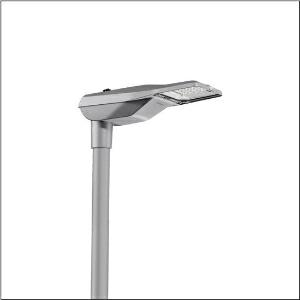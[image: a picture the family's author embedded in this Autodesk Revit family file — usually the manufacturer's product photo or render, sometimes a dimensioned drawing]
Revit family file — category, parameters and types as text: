
# Revit family: streetlight_sl_21_micro___st1_5a_5xe1p43s08db_ce40
name_source: partatom
category: Lighting Fixtures
units: mm (PartAtom-declared; Revit-internal decimal feet)

## family parameters
Cut with Voids When Loaded = No
Host = Face
Light Source = No
Part Type = Normal
Room Calculation Point = No
Round Connector Dimension = Use Diameter
Shared = No

## types (1)
- --- (1 x LED, 5230 lm, 39.1 W, 4000K)
    Apparent Load = 39 VA
    CIE Flux Codes = 22 53 95 100 100
    Color Rendering = 70
    Color Temperature = 4000K
    Default Elevation = 1800 mm
    Description = Streetlight SL 21 micro, mast luminaire, primary light control with lens, of PMMA, primary optical cover: cover, of toughened safety glass, transparent, light distribution: ST1.5a, light emission: direct distribution, primary light characteristic: asymmetric, installation type: side-entry, post-top, LED, High Power LED, rated luminous flux: 5.230lm, luminous efficacy: 134lm/W, light colour: 740, colour temperature: 4000K, control: flexible luminous flux parameterisation, time-dependent luminous flux control, constant luminous flux control, overheat protection, pre-setting: logarithmic dimming characteristic, mains connection: 220..240V, AC, 50/60Hz, start of lifetime: 39W, end of service life: 41W, reduction: 18W, luminaire housing, of diecast aluminium, powder-coated, Siteco® metallic grey (DB 702S), corrosivity category C5 mid according to DIN EN ISO 12944, please order mast flange separately, inclination adjustable: 0°, 5°, 10°, 15°, sealing non-destructively replaceable, multi-level sealing system, length: 528mm, width: 235mm, height: 110mm, mast flange for spigot size: 42mm (side-entry): 5XC10008XM4, 60/48mm (side-entry/post-top): 5XC10108XM2, 76/60mm (side-entry/post-top): 5XC10108XM1, Smart Interface above, protection rating (complete): IP66, insulation class (complete): insulation class II (safety insulation), certification: CE, ENEC, ENEC+, VDE, impact resistance: IK09, permissible operating ambient temperature for outdoor applications: -40..+50°C, standard-compliant lighting for roads and squares, packaging unit: 1 piece

Light Distribution: ST1.5a
    Height = 110 mm
    Lamp = 1 x LED
    Lamp Light Flux = 5230 lm
    Lamp Power = 39.1 W
    Lamp count = 1
    Length = 528 mm
    Luminous efficacy = 134 lm/W
    Manufacturer = Siteco
    ModVariant = No
    Model = 5XE1P43S08DB
    Number of Poles = 1
    OnlyDefault = Yes
    Power Factor = 1
    Product Name = Streetlight SL 21 micro | ST1.5a
    Product group = mast luminaire | pylon top
    ProductGroupID = 6100
    Protection Class = Protection class II
    Protection Degree = IP 66
    RLX_Detail_Level = 1
    RLX_Emergency_Light_Flux = 0 lm
    RLX_Emergency_Type = 0
    RLX_Emergency_Type_DB = No
    RlxData = <blob elided: 102553 chars, md5=652c07a2>
    Socket = socket
    Standby Power = 0 W
    System Light Flux = 5230 lm
    System Power = 39 W
    Type Comments = factory setting: luminous flux: 100 % | dim-lin: 254 | 765 mA
    Type Image = l_1277292.jpg
    URL = http://relux.com
    VarID = @adj_124083
    Voltage = 0 V
    Weight = 0.00 kg
    Width = 235 mm

## geometry (parser evidence)
native form markers: Blend x4, Sweep x11
no freeform markers — native parametric forms only
